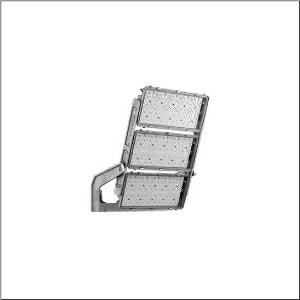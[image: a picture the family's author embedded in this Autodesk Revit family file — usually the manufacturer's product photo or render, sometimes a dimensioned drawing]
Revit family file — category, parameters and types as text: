
# Revit family: floodlight_fl_11_maxi_pro_remote___pl33t_5xa779426t01aa_e8f6
name_source: partatom
category: Lighting Fixtures
units: mm (PartAtom-declared; Revit-internal decimal feet)

## family parameters
Cut with Voids When Loaded = No
Host = Face
Light Source = No
Part Type = Normal
Room Calculation Point = No
Round Connector Dimension = Use Diameter
Shared = No

## types (1)
- --- (1 x LED, 211660 lm, 1539.7 W, 4000K)
    Apparent Load = 1540 VA
    CIE Flux Codes = 27 70 98 100 100
    Color Rendering = 70
    Color Temperature = 4000K
    Default Elevation = 1800 mm
    Description = Floodlight FL 11  maxi  pro Remote floodlight; light control with lens of PMMA; cover panel of toughened safety glass, transparent; light distribution: PL33T, asymmetric direct distribution, LEDcolour temperature: 4000K, rated luminous flux: 211.660lm, colour rendering: CRI > 70, light colour: 740; luminous efficacy: 138lm/W; brightness control: DALI 2 (1 DALI address); with terminal, 8-pole, max. 2.5mm², mains connection: 220..240V/380..400V AC, 50/60Hz, surge voltage resistance: line to ground: 10kV, ECG replaceable separately, no afterglow with DALI off / DMX off command, LED unit replaceable without ESD environment, dustproof LED module, dimming range 10..100%; 1540W floodlight with 2x LED unit of diecast aluminium, coated grey; length: 713mm / width: 651mm / height: 338mm; mounting bracket, of diecast aluminium, uncoated, natural, equipment: Power, protection rating (complete): IP66; insulation class (complete): insulation class I (protective earthing); certification: CE, ENEC, VDE; ball protection: ball impact resistance with accessories, impact resistance: IK07; only for outdoor installations, rated ambient temperature 10°C, permissible operating ambient temperature: -40..+30°C, permissible storage temperature: -40..+85°Cpackaging unit: 1 piece

Light Distribution: PL33T
    Height = 320 mm
    Lamp = 1 x LED
    Lamp Light Flux = 211660 lm
    Lamp Power = 1539.7 W
    Lamp count = 1
    Length = 1002 mm
    Luminous efficacy = 137 lm/W
    Manufacturer = Siteco
    ModVariant = No
    Model = 5XA779426T01AA
    Mounting Place = Ceiling
    Mounting Type = Surface mounted
    Number of Poles = 1
    OnlyDefault = Yes
    Power Factor = 1
    Product Name = Floodlight FL 11 maxi pro Remote | PL33T
    Product group = floodlight | ceiling mounted
    ProductGroupID = 301
    Protection Class = Protection class I
    Protection Degree = IP 66
    RLX_Detail_Level = 1
    RLX_Emergency_Light_Flux = 0 lm
    RLX_Emergency_Type = 0
    RLX_Emergency_Type_DB = No
    RlxData = <blob elided: 52393 chars, md5=92fc8b95>
    Socket = socket
    Standby Power = 0 W
    System Light Flux = 211660 lm
    System Power = 1540 W
    Type Comments = factory setting: luminous flux: 100 % | dim-lin: 254 | 1080 mA
    Type Image = l_1349141.jpg
    URL = http://relux.com
    VarID = @adj_079608
    Voltage = 0 V
    Weight = 0.00 kg
    Width = 655 mm

## geometry (parser evidence)
native form markers: Blend x4, Sweep x12
no freeform markers — native parametric forms only
